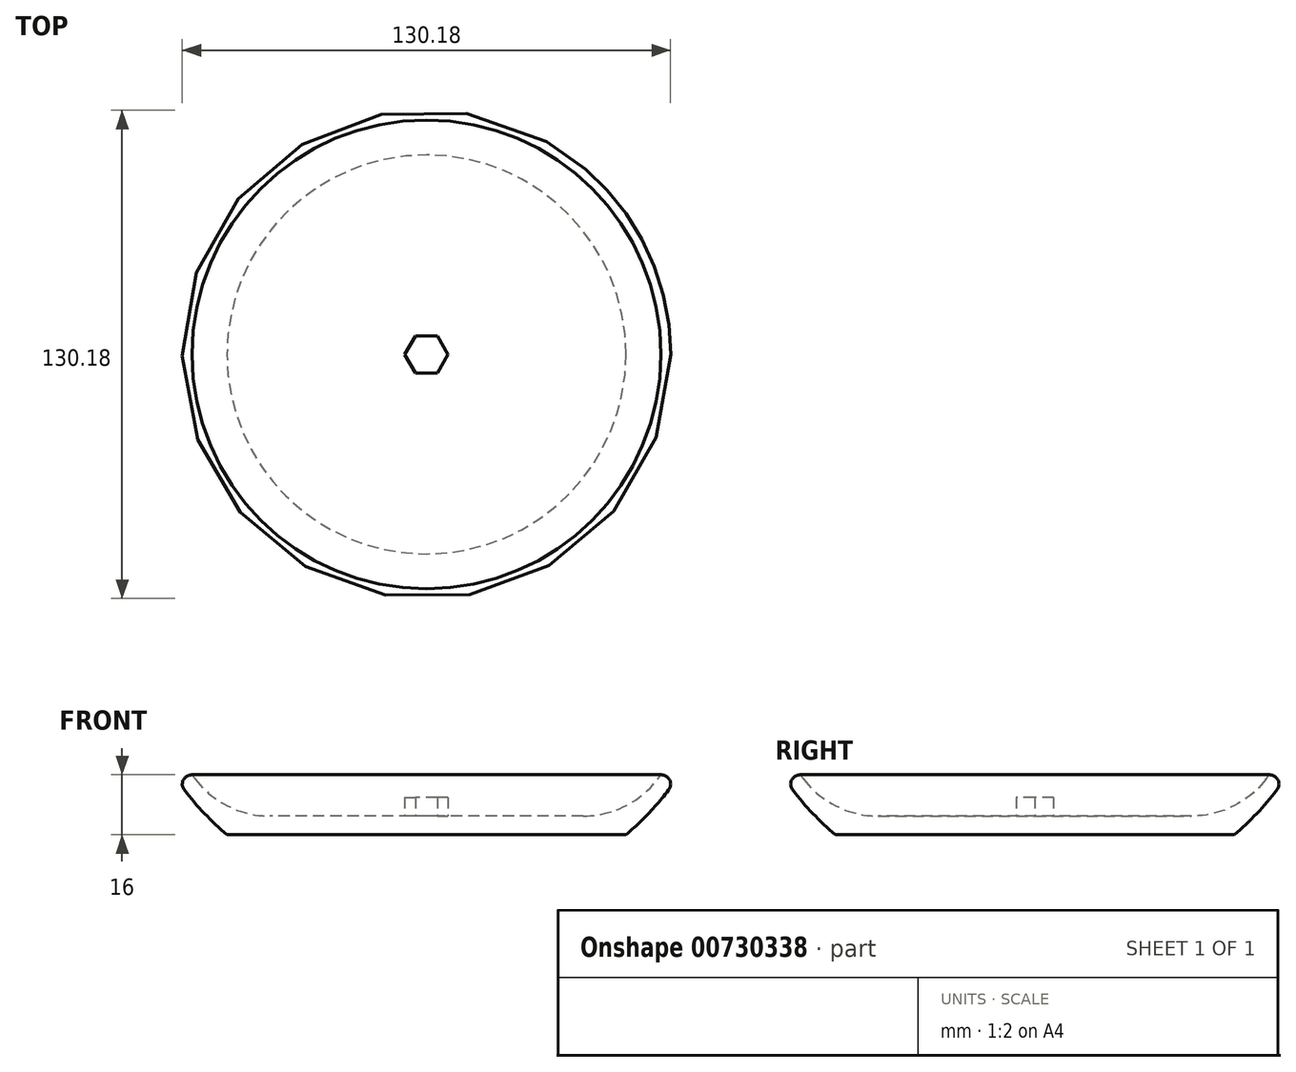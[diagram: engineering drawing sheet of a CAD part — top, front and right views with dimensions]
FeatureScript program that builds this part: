
annotation { "Feature Type Name" : "Feature", "Feature Type Description" : "" }
export const myFeature = defineFeature(function(context is Context, id is Id, definition is map)
    precondition{}
    {
        {
            var Q0;
            Q0=qCreatedBy(makeId("Front.planeOp"),FACE);
            var sketch = newSketch(context, id + "F0", { "sketchPlane" : qUnion([Q0])});
            skArc(sketch, "E0", {"start": v(53.18, -62) * mm, "mid": v(60.87, -54.47) * mm, "end": v(67.5, -46) * mm});
            skArc(sketch, "E1", {"start": v(52.66, -57) * mm, "mid": v(57.84, -51.73) * mm, "end": v(62.5, -46) * mm});
            skLineSegment(sketch, "E2", {"start": v(0, -81.68) * mm, "end": v(0, -77.6) * mm});
            skLineSegment(sketch, "E3", {"start": v(62.5, -46) * mm, "end": v(67.5, -46) * mm});
            skLineSegment(sketch, "E4", {"start": v(0, -62) * mm, "end": v(53.18, -62) * mm});
            skLineSegment(sketch, "E5", {"start": v(0, -57) * mm, "end": v(52.66, -57) * mm});
            skLineSegment(sketch, "E6", {"start": v(0, -57) * mm, "end": v(0, -62) * mm});
            skSolve(sketch);
        }
        {
            var Q0;
            Q0=qCreatedBy(makeId("Front.planeOp"),FACE);
            var sketch = newSketch(context, id + "F1", { "sketchPlane" : qUnion([Q0])});
            skLineSegment(sketch, "E7", {"start": v(0, 75.62) * mm, "end": v(0, -85.07) * mm});
            skSolve(sketch);
        }
        {
            var Q0;
            Q0=makeQuery(id+"F0.imprint","IMPRINT",FACE,{"disambiguationData":[TD([[makeQuery(id+"F0.imprint","IMPRINT",EDGE,{"derivedFrom":sQuery(id+"F0.wireOp",EDGE,"E0")}),1.0]])]});
            var Q1;
            Q1=sQuery(id+"F1.wireOp",EDGE,"E7");
            revolve(context, id + "F2", {"surfaceOperationType" : NewSurfaceOperationType.NEW, "entities" : qUnion([Q0]), "axis" : qUnion([Q1]), "revolveType" : RevolveType.FULL});
        }
        {
            var Q0;
            Q0=makeQuery(id+"F2.opRevolve","SWEPT_FACE",FACE,{"disambiguationData":[OSD([sQuery(id+"F0.wireOp",EDGE,"E5")])]});
            var sketch = newSketch(context, id + "F3", { "sketchPlane" : qUnion([Q0])});
            skCircle(sketch, "E8.cCircle", {"center": v(0, 0) * mm, "radius": 5 * mm, "construction": true});
            skLineSegment(sketch, "E8.0", {"start": v(2.89, -5) * mm, "end": v(-2.89, -5) * mm});
            skLineSegment(sketch, "E8.1", {"start": v(-2.89, -5) * mm, "end": v(-5.77, 0) * mm});
            skLineSegment(sketch, "E8.2", {"start": v(-5.77, 0) * mm, "end": v(-2.89, 5) * mm});
            skLineSegment(sketch, "E8.3", {"start": v(-2.89, 5) * mm, "end": v(2.89, 5) * mm});
            skLineSegment(sketch, "E8.4", {"start": v(2.89, 5) * mm, "end": v(5.77, 0) * mm});
            skLineSegment(sketch, "E8.5", {"start": v(5.77, 0) * mm, "end": v(2.89, -5) * mm});
            skPoint(sketch, "E8.0.midPoint", {"position": v(0, -5) * mm});
            skSolve(sketch);
        }
        {
            var Q0;
            Q0=makeQuery(id+"F3.imprint","IMPRINT",FACE,{"disambiguationData":[TD([[makeQuery(id+"F3.imprint","IMPRINT",EDGE,{"derivedFrom":sQuery(id+"F3.wireOp",EDGE,"E8.0")}),-1.0]])]});
            extrude(context, id + "F4", {"entities" : qUnion([Q0]), "operationType" : NewBodyOperationType.ADD, "depth" : 5 * mm, "offsetDistance" : 25 * mm});
        }
        {
            var Q0;
            Q0=makeQuery(id+"F2.opRevolve","SWEPT_EDGE",EDGE,{"disambiguationData":[OSD([sQuery(id+"F0.wireOp",EDGE,"E0"),sQuery(id+"F0.wireOp",EDGE,"E3")])]});
            fillet(context, id + "F5", {"entities" : qUnion([Q0]), "radius" : 2.5 * mm, "tangentPropagation" : true, "allowEdgeOverflow" : false});
        }
        {
            var Q0;
            Q0=makeQuery(id+"F2.opRevolve","SWEPT_EDGE",EDGE,{"disambiguationData":[OSD([sQuery(id+"F0.wireOp",EDGE,"E1"),sQuery(id+"F0.wireOp",EDGE,"E5")])]});
            fillet(context, id + "F6", {"entities" : qUnion([Q0]), "radius" : 25 * mm, "tangentPropagation" : true, "allowEdgeOverflow" : false});
        }
    });
